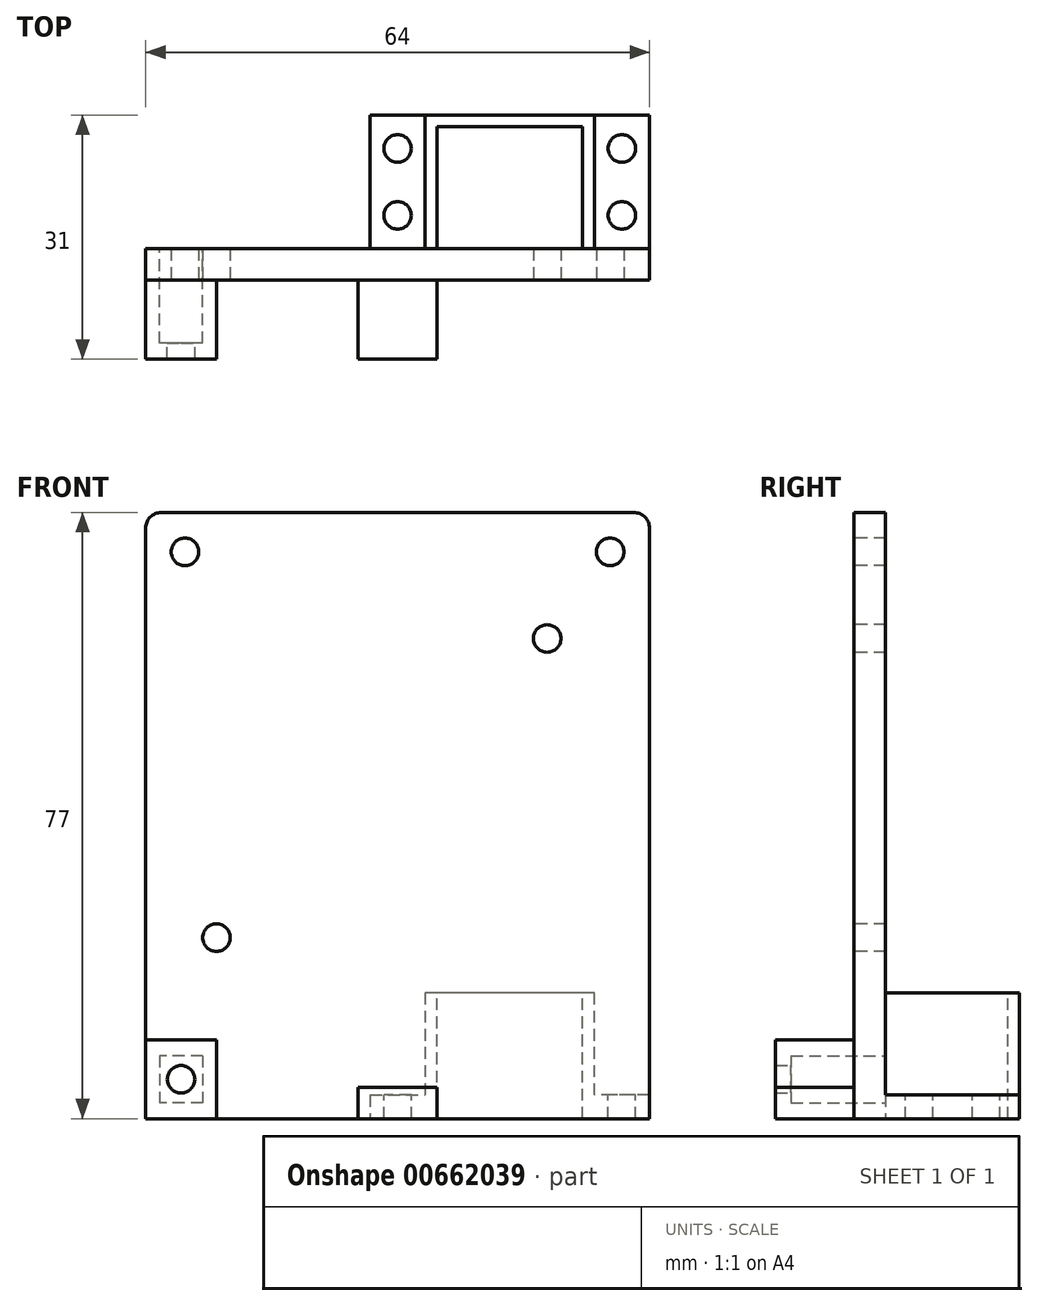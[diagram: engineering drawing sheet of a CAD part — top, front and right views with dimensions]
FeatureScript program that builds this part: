
annotation { "Feature Type Name" : "Feature", "Feature Type Description" : "" }
export const myFeature = defineFeature(function(context is Context, id is Id, definition is map)
    precondition{}
    {
        {
            var Q0;
            Q0=qCreatedBy(makeId("Front.planeOp"),FACE);
            var sketch = newSketch(context, id + "F0", { "sketchPlane" : qUnion([Q0])});
            skLineSegment(sketch, "E0.bottom", {"start": v(-32, 38.5) * mm, "end": v(32, 38.5) * mm});
            skLineSegment(sketch, "E0.top", {"start": v(-32, -38.5) * mm, "end": v(32, -38.5) * mm});
            skLineSegment(sketch, "E0.left", {"start": v(-32, 38.5) * mm, "end": v(-32, -38.5) * mm});
            skLineSegment(sketch, "E0.right", {"start": v(32, 38.5) * mm, "end": v(32, -38.5) * mm});
            skPoint(sketch, "E0.middle", {"position": v(0, 0) * mm});
            skSolve(sketch);
        }
        {
            var Q0;
            Q0=qSketchRegion(id+"F0",true);
            extrude(context, id + "F1", {"entities" : qUnion([Q0]), "depth" : 4 * mm, "offsetDistance" : 25 * mm});
        }
        {
            var Q0;
            Q0=makeQuery(id+"F1.opExtrude","CAP_FACE",FACE,{"disambiguationData":[OSD([sQuery(id+"F0.wireOp",EDGE,"E0.bottom"),sQuery(id+"F0.wireOp",EDGE,"E0.top"),sQuery(id+"F0.wireOp",EDGE,"E0.left"),sQuery(id+"F0.wireOp",EDGE,"E0.right")])],"isStart":false});
            var sketch = newSketch(context, id + "F2", { "sketchPlane" : qUnion([Q0])});
            skLineSegment(sketch, "E1", {"start": v(-32, 38.5) * mm, "end": v(-32, 33.5) * mm});
            skLineSegment(sketch, "E2", {"start": v(-32, 33.5) * mm, "end": v(-27, 33.5) * mm});
            skLineSegment(sketch, "E3", {"start": v(32, 33.5) * mm, "end": v(27, 33.5) * mm});
            skCircle(sketch, "E4", {"center": v(-27, 33.5) * mm, "radius": 1.75 * mm});
            skCircle(sketch, "E5", {"center": v(27, 33.5) * mm, "radius": 1.75 * mm});
            skSolve(sketch);
        }
        {
            var Q0;
            Q0=qSketchRegion(id+"F2",true);
            extrude(context, id + "F3", {"entities" : qUnion([Q0]), "operationType" : NewBodyOperationType.REMOVE, "oppositeDirection" : true, "depth" : 25 * mm, "offsetDistance" : 25 * mm});
        }
        {
            var Q0;
            Q0=makeQuery(id+"F1.opExtrude","CAP_FACE",FACE,{"disambiguationData":[OSD([sQuery(id+"F0.wireOp",EDGE,"E0.bottom"),sQuery(id+"F0.wireOp",EDGE,"E0.top"),sQuery(id+"F0.wireOp",EDGE,"E0.left"),sQuery(id+"F0.wireOp",EDGE,"E0.right")])],"isStart":false});
            var sketch = newSketch(context, id + "F4", { "sketchPlane" : qUnion([Q0])});
            skLineSegment(sketch, "E6", {"start": v(-32, -38.5) * mm, "end": v(0, -38.5) * mm});
            skLineSegment(sketch, "E7", {"start": v(0, -38.5) * mm, "end": v(32, -38.5) * mm});
            skLineSegment(sketch, "E8", {"start": v(0, -38.5) * mm, "end": v(-5, -38.5) * mm});
            skLineSegment(sketch, "E9.bottom", {"start": v(-5, -38.5) * mm, "end": v(5, -38.5) * mm});
            skLineSegment(sketch, "E9.top", {"start": v(-5, -34.5) * mm, "end": v(5, -34.5) * mm});
            skLineSegment(sketch, "E9.left", {"start": v(-5, -38.5) * mm, "end": v(-5, -34.5) * mm});
            skLineSegment(sketch, "E9.right", {"start": v(5, -38.5) * mm, "end": v(5, -34.5) * mm});
            skSolve(sketch);
        }
        {
            var Q0;
            Q0=makeQuery(id+"F4.imprint","IMPRINT",FACE,{"disambiguationData":[TD([[makeQuery(id+"F4.imprint","IMPRINT",EDGE,{"derivedFrom":sQuery(id+"F4.wireOp",EDGE,"E9.top")}),-1.0]])]});
            extrude(context, id + "F5", {"entities" : qUnion([Q0]), "operationType" : NewBodyOperationType.ADD, "depth" : 10 * mm, "offsetDistance" : 25 * mm});
        }
        {
            var Q0;
            Q0=makeQuery(id+"F1.opExtrude","CAP_FACE",FACE,{"disambiguationData":[OSD([sQuery(id+"F0.wireOp",EDGE,"E0.bottom"),sQuery(id+"F0.wireOp",EDGE,"E0.top"),sQuery(id+"F0.wireOp",EDGE,"E0.left"),sQuery(id+"F0.wireOp",EDGE,"E0.right")])],"isStart":false});
            var sketch = newSketch(context, id + "F6", { "sketchPlane" : qUnion([Q0])});
            skLineSegment(sketch, "E10", {"start": v(-32, 38.5) * mm, "end": v(-32, 28.5) * mm});
            skLineSegment(sketch, "E11", {"start": v(0, 28.5) * mm, "end": v(-25.5, 28.5) * mm});
            skPoint(sketch, "E11.startSnap0", {"position": v(0, 38.5) * mm});
            skLineSegment(sketch, "E12", {"start": v(-25.5, 28.5) * mm, "end": v(25.5, 28.5) * mm});
            skLineSegment(sketch, "E13", {"start": v(25.5, 28.5) * mm, "end": v(25.5, 22.5) * mm});
            skLineSegment(sketch, "E14", {"start": v(25.5, -22.5) * mm, "end": v(-25.5, -22.5) * mm});
            skLineSegment(sketch, "E15", {"start": v(-25.5, -22.5) * mm, "end": v(-25.5, 28.5) * mm});
            skLineSegment(sketch, "E16", {"start": v(25.5, 28.5) * mm, "end": v(19, 28.5) * mm});
            skLineSegment(sketch, "E17", {"start": v(25.5, 22.5) * mm, "end": v(19, 22.5) * mm});
            skLineSegment(sketch, "E18", {"start": v(19, 22.5) * mm, "end": v(19, 28.5) * mm});
            skCircle(sketch, "E19", {"center": v(19, 22.5) * mm, "radius": 1.75 * mm});
            skLineSegment(sketch, "E20", {"start": v(-25.5, -22.5) * mm, "end": v(-23, -22.5) * mm});
            skLineSegment(sketch, "E21", {"start": v(-23, -22.5) * mm, "end": v(-23, -15.5) * mm});
            skCircle(sketch, "E22", {"center": v(-23, -15.5) * mm, "radius": 1.75 * mm});
            skLineSegment(sketch, "E23", {"start": v(25.5, 22.5) * mm, "end": v(25.5, -22.5) * mm});
            skSolve(sketch);
        }
        {
            var Q0;
            {var subQ0=sQuery(id+"F6.wireOp",EDGE,"E18");var subQ1=sQuery(id+"F6.wireOp",EDGE,"E17");var subQ2=makeQuery(id+"F6.imprint","INTERSECT",VERTEX,{"derivedFrom":[subQ1,subQ0]});Q0=makeQuery(id+"F6.imprint","IMPRINT",FACE,{"disambiguationData":[TD([[makeQuery(id+"F6.imprint","IMPRINT",EDGE,{"disambiguationData":[TD([[subQ2,1.0]])],"derivedFrom":subQ1}),1.0]])]});}
            var Q1;
            {var subQ0=sQuery(id+"F6.wireOp",EDGE,"E18");var subQ1=sQuery(id+"F6.wireOp",EDGE,"E17");var subQ2=makeQuery(id+"F6.imprint","INTERSECT",VERTEX,{"derivedFrom":[subQ1,subQ0]});Q1=makeQuery(id+"F6.imprint","IMPRINT",FACE,{"disambiguationData":[TD([[makeQuery(id+"F6.imprint","IMPRINT",EDGE,{"disambiguationData":[TD([[subQ2,1.0]])],"derivedFrom":subQ1}),-1.0]])]});}
            var Q2;
            Q2=makeQuery(id+"F6.imprint","IMPRINT",FACE,{"disambiguationData":[TD([[makeQuery(id+"F6.imprint","IMPRINT",EDGE,{"derivedFrom":sQuery(id+"F6.wireOp",EDGE,"E22")}),1.0]])]});
            var Q3;
            {var subQ0=sQuery(id+"F6.wireOp",EDGE,"WzVpFfdy-rS4M-CrLF-odE0-cmMbEIH3Pd6s");var subQ1=sQuery(id+"F6.wireOp",EDGE,"8NUDRCu5-aEot-ui1M-yjk2-xvwixPuLHvAP");var subQ2=makeQuery(id+"F6.imprint","INTERSECT",VERTEX,{"derivedFrom":[subQ1,subQ0]});Q3=makeQuery(id+"F6.imprint","IMPRINT",FACE,{"disambiguationData":[TD([[makeQuery(id+"F6.imprint","IMPRINT",EDGE,{"disambiguationData":[TD([[subQ2,1.0]])],"derivedFrom":subQ1}),-1.0]])]});}
            var Q4;
            {var subQ0=sQuery(id+"F6.wireOp",EDGE,"WzVpFfdy-rS4M-CrLF-odE0-cmMbEIH3Pd6s");var subQ1=sQuery(id+"F6.wireOp",EDGE,"8NUDRCu5-aEot-ui1M-yjk2-xvwixPuLHvAP");var subQ2=makeQuery(id+"F6.imprint","INTERSECT",VERTEX,{"derivedFrom":[subQ1,subQ0]});Q4=makeQuery(id+"F6.imprint","IMPRINT",FACE,{"disambiguationData":[TD([[makeQuery(id+"F6.imprint","IMPRINT",EDGE,{"disambiguationData":[TD([[subQ2,1.0]])],"derivedFrom":subQ1}),1.0]])]});}
            var Q5;
            {var subQ0=sQuery(id+"F6.wireOp",EDGE,"tFdj53bw-FNUA-4jEZ-WwVQ-vJ9Yu2zIjBWe");var subQ1=sQuery(id+"F6.wireOp",EDGE,"PQexaNkZ-5kta-DWHV-akAf-0N8x0B8hL5tD");var subQ2=makeQuery(id+"F6.imprint","INTERSECT",VERTEX,{"derivedFrom":[subQ1,subQ0]});Q5=makeQuery(id+"F6.imprint","IMPRINT",FACE,{"disambiguationData":[TD([[makeQuery(id+"F6.imprint","IMPRINT",EDGE,{"disambiguationData":[TD([[subQ2,1.0]])],"derivedFrom":subQ1}),1.0]])]});}
            var Q6;
            {var subQ0=sQuery(id+"F6.wireOp",EDGE,"tFdj53bw-FNUA-4jEZ-WwVQ-vJ9Yu2zIjBWe");var subQ1=sQuery(id+"F6.wireOp",EDGE,"PQexaNkZ-5kta-DWHV-akAf-0N8x0B8hL5tD");var subQ2=makeQuery(id+"F6.imprint","INTERSECT",VERTEX,{"derivedFrom":[subQ1,subQ0]});Q6=makeQuery(id+"F6.imprint","IMPRINT",FACE,{"disambiguationData":[TD([[makeQuery(id+"F6.imprint","IMPRINT",EDGE,{"disambiguationData":[TD([[subQ2,1.0]])],"derivedFrom":subQ1}),-1.0]])]});}
            extrude(context, id + "F7", {"entities" : qUnion([Q0, Q1, Q2, Q3, Q4, Q5, Q6]), "operationType" : NewBodyOperationType.REMOVE, "oppositeDirection" : true, "depth" : 25 * mm, "offsetDistance" : 25 * mm});
        }
        {
            var Q0;
            Q0=makeQuery(id+"F1.opExtrude","CAP_FACE",FACE,{"disambiguationData":[OSD([sQuery(id+"F0.wireOp",EDGE,"E0.bottom"),sQuery(id+"F0.wireOp",EDGE,"E0.top"),sQuery(id+"F0.wireOp",EDGE,"E0.left"),sQuery(id+"F0.wireOp",EDGE,"E0.right")])],"isStart":true});
            var sketch = newSketch(context, id + "F8", { "sketchPlane" : qUnion([Q0])});
            skLineSegment(sketch, "E24", {"start": v(-32, -38.5) * mm, "end": v(-25, -38.5) * mm});
            skLineSegment(sketch, "E25", {"start": v(-25, -38.5) * mm, "end": v(-3.5, -38.5) * mm});
            skLineSegment(sketch, "E26", {"start": v(-25, -38.5) * mm, "end": v(-25, -22.5) * mm});
            skLineSegment(sketch, "E27", {"start": v(-25, -22.5) * mm, "end": v(-3.5, -22.5) * mm});
            skLineSegment(sketch, "E28", {"start": v(-3.5, -22.5) * mm, "end": v(-3.5, -38.5) * mm});
            skSolve(sketch);
        }
        {
            var Q0;
            Q0=qSketchRegion(id+"F8",true);
            extrude(context, id + "F9", {"entities" : qUnion([Q0]), "operationType" : NewBodyOperationType.ADD, "depth" : 17 * mm, "offsetDistance" : 25 * mm});
        }
        {
            var Q0;
            Q0=makeQuery(id+"F9.opExtrude","SWEPT_FACE",FACE,{"disambiguationData":[OSD([sQuery(id+"F8.wireOp",EDGE,"E27")])]});
            var sketch = newSketch(context, id + "F10", { "sketchPlane" : qUnion([Q0])});
            skLineSegment(sketch, "E29", {"start": v(25, 0) * mm, "end": v(23.5, 0) * mm});
            skLineSegment(sketch, "E30", {"start": v(23.5, 0) * mm, "end": v(23.5, 17) * mm});
            skLineSegment(sketch, "E31", {"start": v(3.5, 0) * mm, "end": v(5, 0) * mm});
            skLineSegment(sketch, "E32", {"start": v(5, 0) * mm, "end": v(5, 17) * mm});
            skLineSegment(sketch, "E33", {"start": v(25, 17) * mm, "end": v(25, 15.5) * mm});
            skLineSegment(sketch, "E34", {"start": v(25, 15.5) * mm, "end": v(3.5, 15.5) * mm});
            skSolve(sketch);
        }
        {
            var Q0;
            {var subQ0=sQuery(id+"F10.wireOp",EDGE,"E30");var subQ3=sQuery(id+"F10.wireOp",EDGE,"E34");var subQ4=makeQuery(id+"F10.imprint","INTERSECT",VERTEX,{"derivedFrom":[subQ0,subQ3]});Q0=makeQuery(id+"F10.imprint","IMPRINT",FACE,{"disambiguationData":[TD([[makeQuery(id+"F10.imprint","IMPRINT",EDGE,{"disambiguationData":[TD([[subQ4,-1.0]])],"derivedFrom":subQ3}),1.0]])]});}
            extrude(context, id + "F11", {"entities" : qUnion([Q0]), "operationType" : NewBodyOperationType.REMOVE, "oppositeDirection" : true, "depth" : 25 * mm, "offsetDistance" : 25 * mm});
        }
        {
            var Q0;
            Q0=makeQuery(id+"F9.opExtrude","SWEPT_FACE",FACE,{"disambiguationData":[OSD([sQuery(id+"F8.wireOp",EDGE,"E26")])]});
            var sketch = newSketch(context, id + "F12", { "sketchPlane" : qUnion([Q0])});
            skLineSegment(sketch, "E35.bottom", {"start": v(0, -38.5) * mm, "end": v(17, -38.5) * mm});
            skLineSegment(sketch, "E35.top", {"start": v(0, -35.5) * mm, "end": v(17, -35.5) * mm});
            skLineSegment(sketch, "E35.left", {"start": v(0, -38.5) * mm, "end": v(0, -35.5) * mm});
            skLineSegment(sketch, "E35.right", {"start": v(17, -38.5) * mm, "end": v(17, -35.5) * mm});
            skSolve(sketch);
        }
        {
            var Q0;
            Q0=qSketchRegion(id+"F12",true);
            extrude(context, id + "F13", {"entities" : qUnion([Q0]), "operationType" : NewBodyOperationType.ADD, "depth" : 7 * mm, "offsetDistance" : 25 * mm});
        }
        {
            var Q0;
            Q0=makeQuery(id+"F9.opExtrude","SWEPT_FACE",FACE,{"disambiguationData":[OSD([sQuery(id+"F8.wireOp",EDGE,"E28")])]});
            var sketch = newSketch(context, id + "F14", { "sketchPlane" : qUnion([Q0])});
            skLineSegment(sketch, "E36.bottom", {"start": v(0, -38.5) * mm, "end": v(-17, -38.5) * mm});
            skLineSegment(sketch, "E36.top", {"start": v(0, -35.5) * mm, "end": v(-17, -35.5) * mm});
            skLineSegment(sketch, "E36.left", {"start": v(0, -38.5) * mm, "end": v(0, -35.5) * mm});
            skLineSegment(sketch, "E36.right", {"start": v(-17, -38.5) * mm, "end": v(-17, -35.5) * mm});
            skSolve(sketch);
        }
        {
            var Q0;
            Q0=qSketchRegion(id+"F14",true);
            extrude(context, id + "F15", {"entities" : qUnion([Q0]), "operationType" : NewBodyOperationType.ADD, "depth" : 7 * mm, "offsetDistance" : 25 * mm});
        }
        {
            var Q0;
            Q0=makeQuery(id+"F15.opExtrude","SWEPT_FACE",FACE,{"disambiguationData":[OSD([sQuery(id+"F14.wireOp",EDGE,"E36.top")])]});
            var sketch = newSketch(context, id + "F16", { "sketchPlane" : qUnion([Q0])});
            skLineSegment(sketch, "E37", {"start": v(0, 0) * mm, "end": v(0, 8.5) * mm});
            skLineSegment(sketch, "E38", {"start": v(0, 8.5) * mm, "end": v(0, 17) * mm});
            skCircle(sketch, "E39", {"center": v(0, 12.75) * mm, "radius": 1.75 * mm});
            skCircle(sketch, "E40", {"center": v(0, 4.25) * mm, "radius": 1.75 * mm});
            skSolve(sketch);
        }
        {
            var Q0;
            {var subQ0=sQuery(id+"F16.wireOp",EDGE,"E39");var subQ1=sQuery(id+"F16.wireOp",EDGE,"E38");var subQ2=makeQuery(id+"F16.imprint","INTERSECT",VERTEX,{"disambiguationData":[OD(0.0)],"derivedFrom":[subQ1,subQ0]});Q0=makeQuery(id+"F16.imprint","IMPRINT",FACE,{"disambiguationData":[TD([[makeQuery(id+"F16.imprint","IMPRINT",EDGE,{"disambiguationData":[TD([[subQ2,-1.0]])],"derivedFrom":subQ1}),-1.0]])]});}
            var Q1;
            {var subQ0=sQuery(id+"F16.wireOp",EDGE,"E39");var subQ1=sQuery(id+"F16.wireOp",EDGE,"E38");var subQ2=makeQuery(id+"F16.imprint","INTERSECT",VERTEX,{"disambiguationData":[OD(0.0)],"derivedFrom":[subQ1,subQ0]});Q1=makeQuery(id+"F16.imprint","IMPRINT",FACE,{"disambiguationData":[TD([[makeQuery(id+"F16.imprint","IMPRINT",EDGE,{"disambiguationData":[TD([[subQ2,-1.0]])],"derivedFrom":subQ1}),1.0]])]});}
            var Q2;
            {var subQ0=sQuery(id+"F16.wireOp",EDGE,"E40");var subQ1=sQuery(id+"F16.wireOp",EDGE,"E37");var subQ2=makeQuery(id+"F16.imprint","INTERSECT",VERTEX,{"disambiguationData":[OD(0.0)],"derivedFrom":[subQ1,subQ0]});Q2=makeQuery(id+"F16.imprint","IMPRINT",FACE,{"disambiguationData":[TD([[makeQuery(id+"F16.imprint","IMPRINT",EDGE,{"disambiguationData":[TD([[subQ2,-1.0]])],"derivedFrom":subQ1}),1.0]])]});}
            var Q3;
            {var subQ0=sQuery(id+"F16.wireOp",EDGE,"E40");var subQ1=sQuery(id+"F16.wireOp",EDGE,"E37");var subQ2=makeQuery(id+"F16.imprint","INTERSECT",VERTEX,{"disambiguationData":[OD(0.0)],"derivedFrom":[subQ1,subQ0]});Q3=makeQuery(id+"F16.imprint","IMPRINT",FACE,{"disambiguationData":[TD([[makeQuery(id+"F16.imprint","IMPRINT",EDGE,{"disambiguationData":[TD([[subQ2,-1.0]])],"derivedFrom":subQ1}),-1.0]])]});}
            extrude(context, id + "F17", {"entities" : qUnion([Q0, Q1, Q2, Q3]), "operationType" : NewBodyOperationType.REMOVE, "oppositeDirection" : true, "depth" : 25 * mm, "offsetDistance" : 25 * mm});
        }
        {
            var Q0;
            Q0=makeQuery(id+"F13.opExtrude","SWEPT_FACE",FACE,{"disambiguationData":[OSD([sQuery(id+"F12.wireOp",EDGE,"E35.top")])]});
            var sketch = newSketch(context, id + "F18", { "sketchPlane" : qUnion([Q0])});
            skLineSegment(sketch, "E41", {"start": v(28.5, 17) * mm, "end": v(28.5, 8.5) * mm});
            skLineSegment(sketch, "E42", {"start": v(28.5, 8.5) * mm, "end": v(28.5, 0) * mm});
            skCircle(sketch, "E43", {"center": v(28.5, 12.75) * mm, "radius": 1.75 * mm});
            skCircle(sketch, "E44", {"center": v(28.5, 4.25) * mm, "radius": 1.75 * mm});
            skSolve(sketch);
        }
        {
            var Q0;
            Q0=qSketchRegion(id+"F18",true);
            extrude(context, id + "F19", {"entities" : qUnion([Q0]), "operationType" : NewBodyOperationType.REMOVE, "oppositeDirection" : true, "depth" : 25 * mm, "offsetDistance" : 25 * mm});
        }
        {
            var Q0;
            Q0=makeQuery(id+"F1.opExtrude","CAP_FACE",FACE,{"disambiguationData":[OSD([sQuery(id+"F0.wireOp",EDGE,"E0.bottom"),sQuery(id+"F0.wireOp",EDGE,"E0.top"),sQuery(id+"F0.wireOp",EDGE,"E0.left"),sQuery(id+"F0.wireOp",EDGE,"E0.right")])],"isStart":false});
            var sketch = newSketch(context, id + "F20", { "sketchPlane" : qUnion([Q0])});
            skLineSegment(sketch, "E45.bottom", {"start": v(-32, -38.5) * mm, "end": v(-23, -38.5) * mm});
            skLineSegment(sketch, "E45.top", {"start": v(-32, -28.5) * mm, "end": v(-23, -28.5) * mm});
            skLineSegment(sketch, "E45.left", {"start": v(-32, -38.5) * mm, "end": v(-32, -28.5) * mm});
            skLineSegment(sketch, "E45.right", {"start": v(-23, -38.5) * mm, "end": v(-23, -28.5) * mm});
            skLineSegment(sketch, "E46", {"start": v(-27.5, -38.5) * mm, "end": v(-27.5, -33.5) * mm});
            skPoint(sketch, "E46.endSnap0", {"position": v(-32, -33.5) * mm});
            skCircle(sketch, "E47", {"center": v(-27.5, -33.5) * mm, "radius": 1.75 * mm});
            skSolve(sketch);
        }
        {
            var Q0;
            Q0=qSketchRegion(id+"F20",true);
            extrude(context, id + "F21", {"entities" : qUnion([Q0]), "operationType" : NewBodyOperationType.ADD, "depth" : 10 * mm, "offsetDistance" : 25 * mm});
        }
        {
            var Q0;
            Q0=makeQuery(id+"F21.boolean.opBoolean","SPLIT",FACE,{"disambiguationData":[TD([makeQuery(id+"F21.opExtrude","SWEPT_FACE",FACE,{"disambiguationData":[OSD([sQuery(id+"F20.wireOp",EDGE,"E47")])]})])],"derivedFrom":makeQuery(id+"F1.opExtrude","CAP_FACE",FACE,{"disambiguationData":[OSD([sQuery(id+"F0.wireOp",EDGE,"E0.bottom"),sQuery(id+"F0.wireOp",EDGE,"E0.top"),sQuery(id+"F0.wireOp",EDGE,"E0.left"),sQuery(id+"F0.wireOp",EDGE,"E0.right")])],"isStart":false})});
            extrude(context, id + "F22", {"entities" : qUnion([Q0]), "operationType" : NewBodyOperationType.REMOVE, "oppositeDirection" : true, "depth" : 25 * mm, "offsetDistance" : 25 * mm});
        }
        {
            var Q0;
            Q0=makeQuery(id+"F11.boolean.opBoolean","MERGE",FACE,{"derivedFrom":[makeQuery(id+"F1.opExtrude","CAP_FACE",FACE,{"disambiguationData":[OSD([sQuery(id+"F0.wireOp",EDGE,"E0.bottom"),sQuery(id+"F0.wireOp",EDGE,"E0.top"),sQuery(id+"F0.wireOp",EDGE,"E0.left"),sQuery(id+"F0.wireOp",EDGE,"E0.right")])],"isStart":true}),makeQuery(id+"F11.opExtrude","SWEPT_FACE",FACE,{"disambiguationData":[OSD([sQuery(id+"F8.wireOp",EDGE,"E27")])]})]});
            var sketch = newSketch(context, id + "F23", { "sketchPlane" : qUnion([Q0])});
            skLineSegment(sketch, "E48.bottom", {"start": v(24.75, -30.5) * mm, "end": v(30.25, -30.5) * mm});
            skLineSegment(sketch, "E48.top", {"start": v(24.75, -36.5) * mm, "end": v(30.25, -36.5) * mm});
            skLineSegment(sketch, "E48.left", {"start": v(24.75, -30.5) * mm, "end": v(24.75, -36.5) * mm});
            skLineSegment(sketch, "E48.right", {"start": v(30.25, -30.5) * mm, "end": v(30.25, -36.5) * mm});
            skPoint(sketch, "E48.middle", {"position": v(27.5, -33.5) * mm});
            skSolve(sketch);
        }
        {
            var Q0;
            Q0=makeQuery(id+"F23.imprint","IMPRINT",FACE,{"disambiguationData":[TD([[makeQuery(id+"F23.imprint","IMPRINT",EDGE,{"derivedFrom":sQuery(id+"F23.wireOp",EDGE,"E48.bottom")}),-1.0]])]});
            extrude(context, id + "F24", {"entities" : qUnion([Q0]), "operationType" : NewBodyOperationType.REMOVE, "oppositeDirection" : true, "depth" : 12 * mm, "offsetDistance" : 25 * mm});
        }
        {
            var Q0;
            Q0=makeQuery(id+"F1.opExtrude","SWEPT_EDGE",EDGE,{"disambiguationData":[OSD([sQuery(id+"F0.wireOp",EDGE,"E0.bottom"),sQuery(id+"F0.wireOp",EDGE,"E0.left")])]});
            var Q1;
            Q1=makeQuery(id+"F1.opExtrude","SWEPT_EDGE",EDGE,{"disambiguationData":[OSD([sQuery(id+"F0.wireOp",EDGE,"E0.bottom"),sQuery(id+"F0.wireOp",EDGE,"E0.right")])]});
            fillet(context, id + "F25", {"entities" : qUnion([Q0, Q1]), "radius" : 2 * mm, "tangentPropagation" : true, "allowEdgeOverflow" : false});
        }
    });
